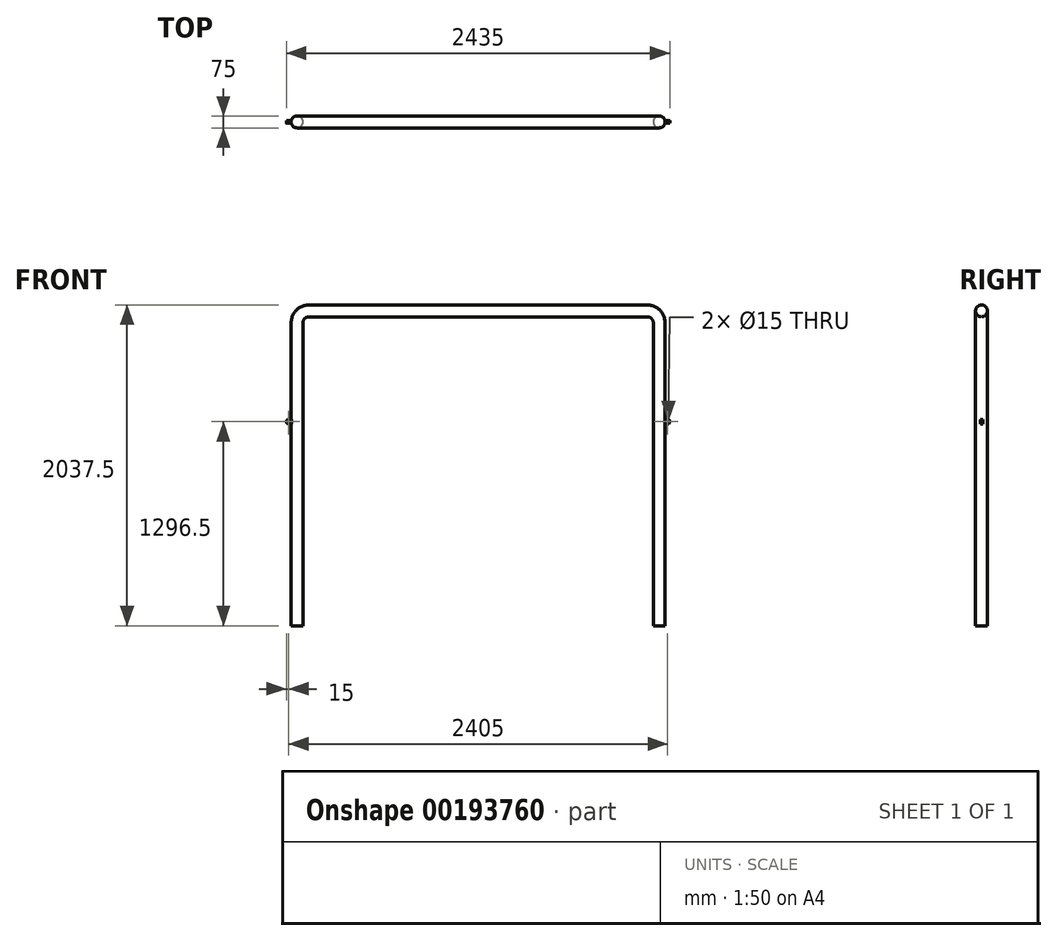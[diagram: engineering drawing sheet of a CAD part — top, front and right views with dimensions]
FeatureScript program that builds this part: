
annotation { "Feature Type Name" : "Feature", "Feature Type Description" : "" }
export const myFeature = defineFeature(function(context is Context, id is Id, definition is map)
    precondition{}
    {
        {
            var Q0;
            Q0=qCreatedBy(makeId("Top.planeOp"),FACE);
            var sketch = newSketch(context, id + "F0", { "sketchPlane" : qUnion([Q0])});
            skCircle(sketch, "E0", {"center": v(-1150, 0) * mm, "radius": 37.5 * mm});
            skCircle(sketch, "E1", {"center": v(1150, 0) * mm, "radius": 37.5 * mm});
            skLineSegment(sketch, "E2", {"start": v(-1150, 0) * mm, "end": v(1150, 0) * mm, "construction": true});
            skSolve(sketch);
        }
        {
            var Q0;
            Q0=qCreatedBy(makeId("Front.planeOp"),FACE);
            var sketch = newSketch(context, id + "F1", { "sketchPlane" : qUnion([Q0])});
            skLineSegment(sketch, "E3", {"start": v(-1150, 0) * mm, "end": v(-1150, 1925) * mm});
            skLineSegment(sketch, "E4", {"start": v(-1075, 2000) * mm, "end": v(1075, 2000) * mm});
            skLineSegment(sketch, "E5", {"start": v(1150, 1925) * mm, "end": v(1150, 0) * mm});
            skPoint(sketch, "E6.visualSharp", {"position": v(1150, 2000) * mm});
            skArc(sketch, "E6.filletArc", {"start": v(1150, 1925) * mm, "mid": v(1128.03, 1978.03) * mm, "end": v(1075, 2000) * mm});
            skPoint(sketch, "E7.visualSharp", {"position": v(-1150, 2000) * mm});
            skArc(sketch, "E7.filletArc", {"start": v(-1075, 2000) * mm, "mid": v(-1128.03, 1978.03) * mm, "end": v(-1150, 1925) * mm});
            skLineSegment(sketch, "E8", {"start": v(0, 0) * mm, "end": v(0, 2223.3) * mm, "construction": true});
            skSolve(sketch);
        }
        {
            var Q0;
            Q0=makeQuery(id+"F0.imprint","IMPRINT",FACE,{"disambiguationData":[TD([[makeQuery(id+"F0.imprint","IMPRINT",EDGE,{"derivedFrom":sQuery(id+"F0.wireOp",EDGE,"E1")}),1.0]])]});
            var Q1;
            Q1=sQuery(id+"F1.wireOp",EDGE,"E5");
            var Q2;
            Q2=sQuery(id+"F1.wireOp",EDGE,"E6.filletArc");
            var Q3;
            Q3=sQuery(id+"F1.wireOp",EDGE,"E4");
            var Q4;
            Q4=sQuery(id+"F1.wireOp",EDGE,"E7.filletArc");
            var Q5;
            Q5=sQuery(id+"F1.wireOp",EDGE,"E3");
            sweep(context, id + "F2", {"profiles" : qUnion([Q0]), "path" : qUnion([Q1, Q2, Q3, Q4, Q5])});
        }
        {
            var Q0;
            Q0=qCreatedBy(makeId("Front.planeOp"),FACE);
            var sketch = newSketch(context, id + "F3", { "sketchPlane" : qUnion([Q0])});
            skLineSegment(sketch, "E9", {"start": v(0, 0) * mm, "end": v(1197.68, 0) * mm, "construction": true});
            skLineSegment(sketch, "E10", {"start": v(1150, 1919.42) * mm, "end": v(1150, -396.21) * mm, "construction": true});
            skLineSegment(sketch, "E11", {"start": v(0, 0) * mm, "end": v(0, 2079.39) * mm, "construction": true});
            skLineSegment(sketch, "E12", {"start": v(-314.1, 1296.5) * mm, "end": v(1888.18, 1296.5) * mm, "construction": true});
            skLineSegment(sketch, "E13.bottom", {"start": v(1150, 1311.5) * mm, "end": v(1202.5, 1311.5) * mm});
            skLineSegment(sketch, "E13.top", {"start": v(1150, 1281.5) * mm, "end": v(1202.5, 1281.5) * mm});
            skLineSegment(sketch, "E13.left", {"start": v(1150, 1311.5) * mm, "end": v(1150, 1281.5) * mm});
            skLineSegment(sketch, "E13.right", {"start": v(1217.5, 1296.5) * mm, "end": v(1217.5, 1296.5) * mm});
            skCircle(sketch, "E14", {"center": v(1202.5, 1296.5) * mm, "radius": 7.5 * mm});
            skPoint(sketch, "E15.visualSharp", {"position": v(1217.5, 1311.5) * mm});
            skArc(sketch, "E15.filletArc", {"start": v(1217.5, 1296.5) * mm, "mid": v(1213.1, 1307.1) * mm, "end": v(1202.5, 1311.5) * mm});
            skPoint(sketch, "E16.visualSharp", {"position": v(1217.5, 1281.5) * mm});
            skArc(sketch, "E16.filletArc", {"start": v(1202.5, 1281.5) * mm, "mid": v(1213.1, 1285.9) * mm, "end": v(1217.5, 1296.5) * mm});
            skLineSegment(sketch, "E17.MirrorCS", {"start": v(-1150, 1311.5) * mm, "end": v(-1202.5, 1311.5) * mm});
            skArc(sketch, "E18.MirrorCS", {"start": v(-1217.5, 1296.5) * mm, "mid": v(-1213.1, 1307.1) * mm, "end": v(-1202.5, 1311.5) * mm});
            skArc(sketch, "E19.MirrorCS", {"start": v(-1202.5, 1281.5) * mm, "mid": v(-1213.1, 1285.9) * mm, "end": v(-1217.5, 1296.5) * mm});
            skLineSegment(sketch, "E20.MirrorCS", {"start": v(-1150, 1281.5) * mm, "end": v(-1202.5, 1281.5) * mm});
            skCircle(sketch, "E21.MirrorC", {"center": v(-1202.5, 1296.5) * mm, "radius": 7.5 * mm});
            skLineSegment(sketch, "E22", {"start": v(-1150, 1311.5) * mm, "end": v(-1150, 1281.5) * mm});
            skSolve(sketch);
        }
        {
            var Q0;
            Q0 = qSketchRegion(id + "F3", true);
            extrude(context, id + "F4", {"entities" : qUnion([Q0]), "operationType" : NewBodyOperationType.ADD, "depth" : 8.33 * mm, "hasSecondDirection" : true, "secondDirectionOppositeDirection" : true, "secondDirectionDepth" : 8.33 * mm});
        }
    });
